# Revit family: NBS_HeatraeSadia_InstntnsWtrHtrsPckgdPltHeatExchngrs_Hi-MaxStoreHeatInterfaceUnit
name_source: partatom
category: Plumbing Fixtures
revit_build: Autodesk Revit 2014 (Build: 20130709_2115(x64)
units: mm (PartAtom-declared; Revit-internal decimal feet)

## types (4) — shared parameters
Arrangement = Instantaneous
AssetType = Fixed
CentralHeatingExpansionVesselVolume = 8 L
Connections = ¾" BSP male
Description = Heat interface unit
DurationUnit = year
Features = Compact design, no need for boiler flues, suitable for single and dual zone heating systems, scale reducing feature
Fixing = Wall fixed
HeatInterfaceUnitMaterial = NBS_Concept
Height = 791.7 mm
IfcExportAs = IfcBoilerType
IfcExportType = WATER
IsWaterStorageHeater = No
Length = 620 mm  [stored 2.03412 ft]
ManufacturerName = Heatrae Sadia
ManufacturerURL = www.heatraesadia.com
ModelNumber = 95:050:203
NBSCertification = http://www.nationalbimlibrary.com
NBSDescription = Instantaneous water heaters, packaged plate heat exchangers
NBSReference = 90-15-35/420
NominalHeight = 845 mm
NominalLength = 620 mm  [stored 2.03412 ft]
NominalWidth = 220 mm
OutletTemperatureRange = 90
PressureRating = 3-10 bar
PrimaryFlowRate = 575 L/hour
PrimaryMedium = Medium temperature hot water
ProductInformation = www.elsonhotwater.co.uk/documents/Heat_Interface_Units_-_Issue_2.pdf
Rating = Heat exchanger: 13.40 kW
SafetyFeatures = Central heating safety valve with tundish
SecondaryMedium = Water
Size = 845 x 620 x 220 mm
Uniclass2015Description = Instantaneous plate heat exchangers
Uniclass2015Reference = Pr_60_60_38_42
Uniclass2015Version = Products v1.1
Version = 1
WarrantyDurationLabor = 2
WarrantyDurationParts = 2
WarrantyDurationUnit = year
WaterStorageCapacity = 0
Width = 265 mm  [stored 0.869423 ft]
zero-valued in all types: CWFU, HWFU, HeatOutput, NominalEfficiency, NominalEnergyConsumption, NominalPartLoadRatio, WFU

## per-type parameters (varying)
| type | Accessories | BIMObjectName | ModelReference | Name | PackageUnit | Weight |
| CB-1Z | First fix rail, Programmable room thermostat with DHW time control, Outer casing | NBS_HeatraeSadia_InstantaneousWaterHeatersPackagedPlateHeatExchangers_Hi-MaxStoreHeatInterfaceUnit-CB-1Z | Hi-Max Store Heat Interface Unit - CB-1Z | InstantaneousWaterHeatersPackagedPlateHeatExchangers_Hi-MaxStoreHeatInterfaceUnit-CB-1Z_HeatraeSadia | Heat interface unit with plate heat exchanger and one heating zone | 25 |
| CB-1Z-DC | First fix rail, Programmable room thermostat with DHW time control, Outer casing | NBS_HeatraeSadia_InstantaneousWaterHeatersPackagedPlateHeatExchangers_Hi-MaxStoreHeatInterfaceUnit-CB-1Z-DC | Hi-Max Store Heat Interface Unit - CB-1Z-DC | InstantaneousWaterHeatersPackagedPlateHeatExchangers_Hi-MaxStoreHeatInterfaceUnit-CB-1Z-DC_HeatraeSadia | Heat interface unit with plate heat exchanger and one heating zone with a district control valve | 26 |
| CB-2Z | First fix rail, Programmable room thermostat with DHW time control, Programmable room thermostat for second heating zone 2, Outer casing | NBS_HeatraeSadia_InstantaneousWaterHeatersPackagedPlateHeatExchangers_Hi-MaxStoreHeatInterfaceUnit-CB-2Z | Hi-Max Store Heat Interface Unit - CB-2Z | InstantaneousWaterHeatersPackagedPlateHeatExchangers_Hi-MaxStoreHeatInterfaceUnit-CB-2Z_HeatraeSadia | Heat interface unit with plate heat exchanger and two heating zones | 26 |
| CB-2Z-DC | First fix rail, Programmable room thermostat with DHW time control, Programmable room thermostat for second heating zone 2, Outer casing | NBS_HeatraeSadia_InstantaneousWaterHeatersPackagedPlateHeatExchangers_Hi-MaxStoreHeatInterfaceUnit-CB-2Z-DC | Hi-Max Store Heat Interface Unit - CB-2Z-DC | InstantaneousWaterHeatersPackagedPlateHeatExchangers_Hi-MaxStoreHeatInterfaceUnit-CB-2Z-DC_HeatraeSadia | Heat interface unit with plate heat exchanger and two heating zones with a district control valve | 27 |

note: [stored X ft] marks values corroborated as IEEE doubles in the binary element streams (Revit-internal decimal feet)

## geometry (parser evidence)
native form markers: Sweep x1
no freeform markers — native parametric forms only
